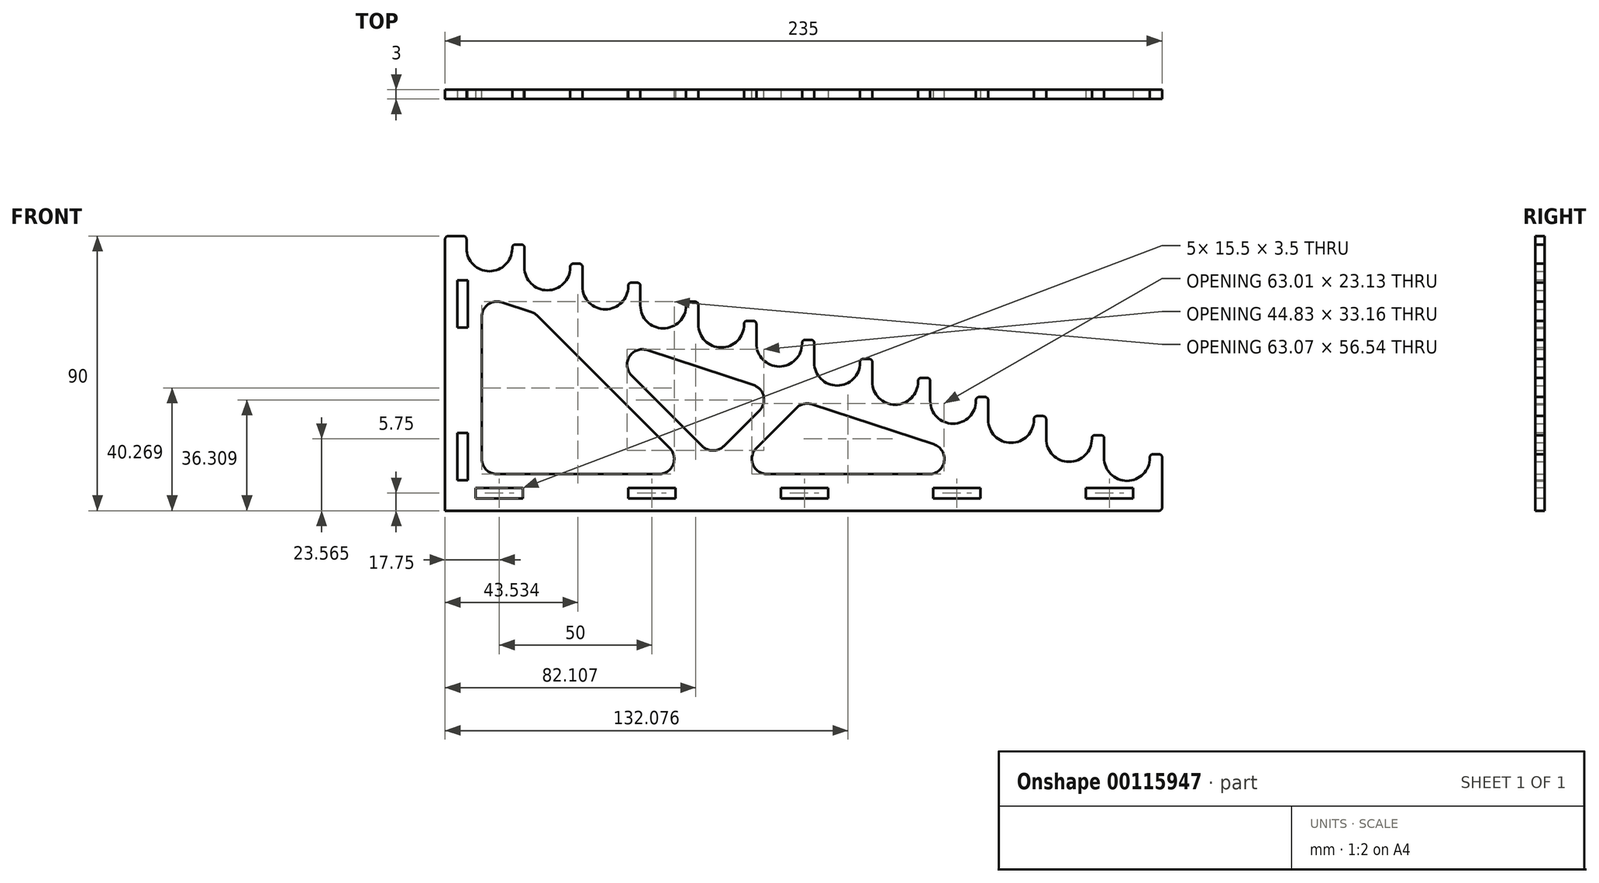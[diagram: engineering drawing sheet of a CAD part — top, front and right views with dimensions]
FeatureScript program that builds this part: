
annotation { "Feature Type Name" : "Feature", "Feature Type Description" : "" }
export const myFeature = defineFeature(function(context is Context, id is Id, definition is map)
    precondition{}
    {
        {
            var Q0;
            Q0=qCreatedBy(makeId("Front.planeOp"),FACE);
            var sketch = newSketch(context, id + "F0", { "sketchPlane" : qUnion([Q0])});
            skLineSegment(sketch, "E0", {"start": v(0, 0) * mm, "end": v(235, 0) * mm});
            skLineSegment(sketch, "E1", {"start": v(0, 0) * mm, "end": v(0, 90) * mm});
            skLineSegment(sketch, "E2", {"start": v(7, 90) * mm, "end": v(239.67, 13.52) * mm, "construction": true});
            skArc(sketch, "E3", {"start": v(7, 86) * mm, "mid": v(14.5, 78.5) * mm, "end": v(22, 86) * mm});
            skLineSegment(sketch, "E4", {"start": v(235, 17.53) * mm, "end": v(235, 0) * mm});
            skLineSegment(sketch, "E5", {"start": v(6, 90) * mm, "end": v(0, 90) * mm});
            skLineSegment(sketch, "E6", {"start": v(7, 86) * mm, "end": v(7, 89) * mm});
            skLineSegment(sketch, "E7.0", {"start": v(12, 17) * mm, "end": v(12, 63.56) * mm});
            skLineSegment(sketch, "E8.0", {"start": v(17, 12) * mm, "end": v(70.1, 12) * mm});
            skLineSegment(sketch, "E9.0", {"start": v(18.56, 68.3) * mm, "end": v(28.3, 65.1) * mm});
            skArc(sketch, "E10.filletArc", {"start": v(18.56, 68.3) * mm, "mid": v(14.07, 67.6) * mm, "end": v(12, 63.56) * mm});
            skArc(sketch, "E11.filletArc", {"start": v(12, 17) * mm, "mid": v(13.46, 13.46) * mm, "end": v(17, 12) * mm});
            skArc(sketch, "E12.filletArc", {"start": v(158.64, 12) * mm, "mid": v(163.58, 16.2) * mm, "end": v(160.2, 21.75) * mm});
            skLineSegment(sketch, "E13.1.0.0", {"start": v(26, 79.76) * mm, "end": v(26, 83.76) * mm});
            skArc(sketch, "E13.1.0.1", {"start": v(26, 79.76) * mm, "mid": v(33.5, 72.26) * mm, "end": v(41, 79.76) * mm});
            skLineSegment(sketch, "E13.2.0.0", {"start": v(45, 73.51) * mm, "end": v(45, 77.51) * mm});
            skArc(sketch, "E13.2.0.1", {"start": v(45, 73.51) * mm, "mid": v(52.5, 66.01) * mm, "end": v(60, 73.51) * mm});
            skLineSegment(sketch, "E13.direction1", {"start": v(7, 86) * mm, "end": v(26, 79.76) * mm, "construction": true});
            skLineSegment(sketch, "E14.0.3.0", {"start": v(64, 67.27) * mm, "end": v(64, 71.27) * mm});
            skArc(sketch, "E14.3.3.0", {"start": v(64, 67.27) * mm, "mid": v(71.5, 59.77) * mm, "end": v(79, 67.27) * mm});
            skLineSegment(sketch, "E14.0.4.0", {"start": v(83, 61.02) * mm, "end": v(83, 65.02) * mm});
            skArc(sketch, "E14.3.4.0", {"start": v(83, 61.02) * mm, "mid": v(90.5, 53.52) * mm, "end": v(98, 61.02) * mm});
            skLineSegment(sketch, "E14.0.5.0", {"start": v(102, 54.78) * mm, "end": v(102, 58.78) * mm});
            skArc(sketch, "E14.3.5.0", {"start": v(102, 54.78) * mm, "mid": v(109.5, 47.28) * mm, "end": v(117, 54.78) * mm});
            skLineSegment(sketch, "E14.0.6.0", {"start": v(121, 48.53) * mm, "end": v(121, 52.53) * mm});
            skArc(sketch, "E14.3.6.0", {"start": v(121, 48.53) * mm, "mid": v(128.5, 41.03) * mm, "end": v(136, 48.53) * mm});
            skLineSegment(sketch, "E14.0.7.0", {"start": v(140, 42.29) * mm, "end": v(140, 46.29) * mm});
            skArc(sketch, "E14.3.7.0", {"start": v(140, 42.29) * mm, "mid": v(147.5, 34.79) * mm, "end": v(155, 42.29) * mm});
            skLineSegment(sketch, "E14.0.8.0", {"start": v(159, 36.04) * mm, "end": v(159, 40.04) * mm});
            skArc(sketch, "E14.3.8.0", {"start": v(159, 36.04) * mm, "mid": v(166.5, 28.54) * mm, "end": v(174, 36.04) * mm});
            skLineSegment(sketch, "E14.0.9.0", {"start": v(178, 29.8) * mm, "end": v(178, 33.8) * mm});
            skArc(sketch, "E14.3.9.0", {"start": v(178, 29.8) * mm, "mid": v(185.5, 22.3) * mm, "end": v(193, 29.8) * mm});
            skLineSegment(sketch, "E14.0.10.0", {"start": v(197, 23.55) * mm, "end": v(197, 27.55) * mm});
            skArc(sketch, "E14.3.10.0", {"start": v(197, 23.55) * mm, "mid": v(204.5, 16.05) * mm, "end": v(212, 23.55) * mm});
            skLineSegment(sketch, "E14.0.11.0", {"start": v(216, 17.3) * mm, "end": v(216, 21.3) * mm});
            skArc(sketch, "E14.3.11.0", {"start": v(216, 17.3) * mm, "mid": v(223.5, 9.8) * mm, "end": v(231, 17.3) * mm});
            skLineSegment(sketch, "E15", {"start": v(235, 18.53) * mm, "end": v(12.69, 91.6) * mm, "construction": true});
            skLineSegment(sketch, "E16", {"start": v(234, 18.53) * mm, "end": v(232, 18.53) * mm});
            skLineSegment(sketch, "E17", {"start": v(231, 17.53) * mm, "end": v(231, 17.3) * mm});
            skLineSegment(sketch, "E18", {"start": v(216, 21.3) * mm, "end": v(216, 23.78) * mm});
            skLineSegment(sketch, "E19", {"start": v(215, 24.78) * mm, "end": v(213, 24.78) * mm});
            skLineSegment(sketch, "E20", {"start": v(212, 23.78) * mm, "end": v(212, 23.55) * mm});
            skLineSegment(sketch, "E21", {"start": v(197, 27.55) * mm, "end": v(197, 30.02) * mm});
            skLineSegment(sketch, "E22", {"start": v(196, 31.02) * mm, "end": v(194, 31.02) * mm});
            skLineSegment(sketch, "E23", {"start": v(193, 30.02) * mm, "end": v(193, 29.8) * mm});
            skLineSegment(sketch, "E24", {"start": v(178, 33.8) * mm, "end": v(178, 36.27) * mm});
            skLineSegment(sketch, "E25", {"start": v(177, 37.27) * mm, "end": v(175, 37.27) * mm});
            skLineSegment(sketch, "E26", {"start": v(174, 36.27) * mm, "end": v(174, 36.04) * mm});
            skLineSegment(sketch, "E27", {"start": v(159, 40.04) * mm, "end": v(159, 42.51) * mm});
            skLineSegment(sketch, "E28", {"start": v(158, 43.51) * mm, "end": v(156, 43.51) * mm});
            skLineSegment(sketch, "E29", {"start": v(155, 42.51) * mm, "end": v(155, 42.29) * mm});
            skLineSegment(sketch, "E30", {"start": v(140, 46.29) * mm, "end": v(140, 48.76) * mm});
            skLineSegment(sketch, "E31", {"start": v(139, 49.76) * mm, "end": v(137, 49.76) * mm});
            skLineSegment(sketch, "E32", {"start": v(136, 48.76) * mm, "end": v(136, 48.53) * mm});
            skLineSegment(sketch, "E33", {"start": v(121, 52.53) * mm, "end": v(121, 55) * mm});
            skLineSegment(sketch, "E34", {"start": v(120, 56) * mm, "end": v(118, 56) * mm});
            skLineSegment(sketch, "E35", {"start": v(117, 55) * mm, "end": v(117, 54.78) * mm});
            skLineSegment(sketch, "E36", {"start": v(102, 58.78) * mm, "end": v(102, 61.25) * mm});
            skLineSegment(sketch, "E37", {"start": v(101, 62.25) * mm, "end": v(99, 62.24) * mm});
            skLineSegment(sketch, "E38", {"start": v(98, 61.24) * mm, "end": v(98, 61.02) * mm});
            skLineSegment(sketch, "E39", {"start": v(83, 65.02) * mm, "end": v(83, 67.5) * mm});
            skLineSegment(sketch, "E40", {"start": v(82, 68.5) * mm, "end": v(80, 68.5) * mm});
            skLineSegment(sketch, "E41", {"start": v(79, 67.5) * mm, "end": v(79, 67.27) * mm});
            skLineSegment(sketch, "E42", {"start": v(64, 71.27) * mm, "end": v(64, 73.74) * mm});
            skLineSegment(sketch, "E43", {"start": v(63, 74.74) * mm, "end": v(61, 74.73) * mm});
            skLineSegment(sketch, "E44", {"start": v(60, 73.73) * mm, "end": v(60, 73.51) * mm});
            skLineSegment(sketch, "E45", {"start": v(45, 77.51) * mm, "end": v(45, 79.98) * mm});
            skLineSegment(sketch, "E46", {"start": v(44, 80.98) * mm, "end": v(42, 80.97) * mm});
            skLineSegment(sketch, "E47", {"start": v(41, 79.97) * mm, "end": v(41, 79.76) * mm});
            skLineSegment(sketch, "E48", {"start": v(26, 83.76) * mm, "end": v(26, 86.23) * mm});
            skLineSegment(sketch, "E49", {"start": v(25, 87.23) * mm, "end": v(23, 87.22) * mm});
            skLineSegment(sketch, "E50", {"start": v(22, 86.22) * mm, "end": v(22, 86) * mm});
            skPoint(sketch, "E51.visualSharp", {"position": v(235, 18.53) * mm});
            skArc(sketch, "E51.filletArc", {"start": v(235, 17.53) * mm, "mid": v(234.7, 18.24) * mm, "end": v(234, 18.53) * mm});
            skPoint(sketch, "E52.visualSharp", {"position": v(231, 18.53) * mm});
            skArc(sketch, "E52.filletArc", {"start": v(232, 18.53) * mm, "mid": v(231.3, 18.24) * mm, "end": v(231, 17.53) * mm});
            skPoint(sketch, "E53.visualSharp", {"position": v(216, 24.78) * mm});
            skArc(sketch, "E53.filletArc", {"start": v(216, 23.78) * mm, "mid": v(215.7, 24.49) * mm, "end": v(215, 24.78) * mm});
            skPoint(sketch, "E54.visualSharp", {"position": v(212, 24.78) * mm});
            skArc(sketch, "E54.filletArc", {"start": v(213, 24.78) * mm, "mid": v(212.3, 24.49) * mm, "end": v(212, 23.78) * mm});
            skPoint(sketch, "E55.visualSharp", {"position": v(197, 31.02) * mm});
            skArc(sketch, "E55.filletArc", {"start": v(197, 30.02) * mm, "mid": v(196.7, 30.73) * mm, "end": v(196, 31.02) * mm});
            skPoint(sketch, "E56.visualSharp", {"position": v(193, 31.02) * mm});
            skArc(sketch, "E56.filletArc", {"start": v(194, 31.02) * mm, "mid": v(193.3, 30.73) * mm, "end": v(193, 30.02) * mm});
            skPoint(sketch, "E57.visualSharp", {"position": v(178, 37.27) * mm});
            skArc(sketch, "E57.filletArc", {"start": v(178, 36.27) * mm, "mid": v(177.7, 36.98) * mm, "end": v(177, 37.27) * mm});
            skPoint(sketch, "E58.visualSharp", {"position": v(174, 37.27) * mm});
            skArc(sketch, "E58.filletArc", {"start": v(175, 37.27) * mm, "mid": v(174.3, 36.98) * mm, "end": v(174, 36.27) * mm});
            skPoint(sketch, "E59.visualSharp", {"position": v(159, 43.51) * mm});
            skArc(sketch, "E59.filletArc", {"start": v(159, 42.51) * mm, "mid": v(158.7, 43.22) * mm, "end": v(158, 43.51) * mm});
            skPoint(sketch, "E60.visualSharp", {"position": v(155, 43.51) * mm});
            skArc(sketch, "E60.filletArc", {"start": v(156, 43.51) * mm, "mid": v(155.3, 43.22) * mm, "end": v(155, 42.51) * mm});
            skPoint(sketch, "E61.visualSharp", {"position": v(140, 49.76) * mm});
            skArc(sketch, "E61.filletArc", {"start": v(140, 48.76) * mm, "mid": v(139.7, 49.47) * mm, "end": v(139, 49.76) * mm});
            skPoint(sketch, "E62.visualSharp", {"position": v(136, 49.76) * mm});
            skArc(sketch, "E62.filletArc", {"start": v(137, 49.76) * mm, "mid": v(136.3, 49.47) * mm, "end": v(136, 48.76) * mm});
            skPoint(sketch, "E63.visualSharp", {"position": v(121, 56) * mm});
            skArc(sketch, "E63.filletArc", {"start": v(121, 55) * mm, "mid": v(120.7, 55.71) * mm, "end": v(120, 56) * mm});
            skPoint(sketch, "E64.visualSharp", {"position": v(117, 56) * mm});
            skArc(sketch, "E64.filletArc", {"start": v(118, 56) * mm, "mid": v(117.3, 55.71) * mm, "end": v(117, 55) * mm});
            skPoint(sketch, "E65.visualSharp", {"position": v(102, 62.25) * mm});
            skArc(sketch, "E65.filletArc", {"start": v(102, 61.25) * mm, "mid": v(101.7, 61.95) * mm, "end": v(101, 62.25) * mm});
            skPoint(sketch, "E66.visualSharp", {"position": v(98, 62.23) * mm});
            skArc(sketch, "E66.filletArc", {"start": v(99, 62.24) * mm, "mid": v(98.3, 61.94) * mm, "end": v(98, 61.24) * mm});
            skPoint(sketch, "E67.visualSharp", {"position": v(83, 68.5) * mm});
            skArc(sketch, "E67.filletArc", {"start": v(83, 67.5) * mm, "mid": v(82.7, 68.2) * mm, "end": v(82, 68.5) * mm});
            skPoint(sketch, "E68.visualSharp", {"position": v(79, 68.5) * mm});
            skArc(sketch, "E68.filletArc", {"start": v(80, 68.5) * mm, "mid": v(79.3, 68.2) * mm, "end": v(79, 67.5) * mm});
            skPoint(sketch, "E69.visualSharp", {"position": v(64, 74.74) * mm});
            skArc(sketch, "E69.filletArc", {"start": v(64, 73.74) * mm, "mid": v(63.7, 74.44) * mm, "end": v(63, 74.74) * mm});
            skPoint(sketch, "E70.visualSharp", {"position": v(60, 74.72) * mm});
            skArc(sketch, "E70.filletArc", {"start": v(61, 74.73) * mm, "mid": v(60.3, 74.43) * mm, "end": v(60, 73.73) * mm});
            skPoint(sketch, "E71.visualSharp", {"position": v(45, 80.98) * mm});
            skArc(sketch, "E71.filletArc", {"start": v(45, 79.98) * mm, "mid": v(44.7, 80.69) * mm, "end": v(44, 80.98) * mm});
            skPoint(sketch, "E72.visualSharp", {"position": v(41, 80.97) * mm});
            skArc(sketch, "E72.filletArc", {"start": v(42, 80.97) * mm, "mid": v(41.3, 80.68) * mm, "end": v(41, 79.97) * mm});
            skPoint(sketch, "E73.visualSharp", {"position": v(26, 87.23) * mm});
            skArc(sketch, "E73.filletArc", {"start": v(26, 86.23) * mm, "mid": v(25.7, 86.93) * mm, "end": v(25, 87.23) * mm});
            skPoint(sketch, "E74.visualSharp", {"position": v(22, 87.21) * mm});
            skArc(sketch, "E74.filletArc", {"start": v(23, 87.22) * mm, "mid": v(22.3, 86.92) * mm, "end": v(22, 86.22) * mm});
            skPoint(sketch, "E75.visualSharp", {"position": v(7, 90) * mm});
            skArc(sketch, "E75.filletArc", {"start": v(7, 89) * mm, "mid": v(6.7, 89.7) * mm, "end": v(6, 90) * mm});
            skLineSegment(sketch, "E76", {"start": v(87.82, 12) * mm, "end": v(37.86, 61.96) * mm, "construction": true});
            skLineSegment(sketch, "E77", {"start": v(87.82, 12) * mm, "end": v(113.06, 37.24) * mm, "construction": true});
            skLineSegment(sketch, "E78.0", {"start": v(73.63, 20.54) * mm, "end": v(30.27, 63.89) * mm});
            skLineSegment(sketch, "E79.0", {"start": v(90.74, 14.74) * mm, "end": v(90.65, 14.83) * mm});
            skLineSegment(sketch, "E80.0", {"start": v(91.36, 21.2) * mm, "end": v(103.06, 32.9) * mm});
            skLineSegment(sketch, "E81.0", {"start": v(102.01, 20.54) * mm, "end": v(115.15, 33.67) * mm});
            skLineSegment(sketch, "E82.trimOffspring", {"start": v(66.22, 52.64) * mm, "end": v(101.09, 41.18) * mm});
            skLineSegment(sketch, "E83.trimOffspring", {"start": v(105.55, 12) * mm, "end": v(158.64, 12) * mm});
            skLineSegment(sketch, "E84.trimOffspring", {"start": v(84.29, 21.2) * mm, "end": v(61.12, 44.36) * mm});
            skLineSegment(sketch, "E85.trimOffspring", {"start": v(120.24, 34.88) * mm, "end": v(160.2, 21.75) * mm});
            skPoint(sketch, "E86.visualSharp", {"position": v(29.43, 64.73) * mm});
            skArc(sketch, "E86.filletArc", {"start": v(30.27, 63.89) * mm, "mid": v(29.36, 64.61) * mm, "end": v(28.3, 65.1) * mm});
            skPoint(sketch, "E87.visualSharp", {"position": v(46.28, 59.2) * mm});
            skArc(sketch, "E87.filletArc", {"start": v(66.22, 52.64) * mm, "mid": v(60.4, 50.51) * mm, "end": v(61.12, 44.36) * mm});
            skPoint(sketch, "E88.visualSharp", {"position": v(108.8, 38.64) * mm});
            skArc(sketch, "E88.filletArc", {"start": v(103.06, 32.9) * mm, "mid": v(104.39, 37.59) * mm, "end": v(101.09, 41.18) * mm});
            skPoint(sketch, "E89.visualSharp", {"position": v(117.32, 35.84) * mm});
            skArc(sketch, "E89.filletArc", {"start": v(120.24, 34.88) * mm, "mid": v(117.52, 35) * mm, "end": v(115.15, 33.67) * mm});
            skPoint(sketch, "E90.visualSharp", {"position": v(93.48, 12) * mm});
            skArc(sketch, "E90.filletArc", {"start": v(102.01, 20.54) * mm, "mid": v(100.93, 15.09) * mm, "end": v(105.55, 12) * mm});
            skPoint(sketch, "E91.visualSharp", {"position": v(87.82, 17.66) * mm});
            skArc(sketch, "E91.filletArc", {"start": v(84.29, 21.2) * mm, "mid": v(87.82, 19.73) * mm, "end": v(91.36, 21.2) * mm});
            skPoint(sketch, "E92.visualSharp", {"position": v(82.16, 12) * mm});
            skArc(sketch, "E92.filletArc", {"start": v(70.1, 12) * mm, "mid": v(74.71, 15.09) * mm, "end": v(73.63, 20.54) * mm});
            skSolve(sketch);
        }
        {
            var Q0;
            Q0=qSketchRegion(id+"F0",true);
            extrude(context, id + "F1", {"entities" : qUnion([Q0]), "depth" : 3 * mm});
        }
        {
            var Q0;
            Q0=makeQuery(id+"F1.opExtrude","SWEPT_EDGE",EDGE,{"disambiguationData":[OSD([sQuery(id+"F0.wireOp",EDGE,"E5"),sQuery(id+"F0.wireOp",EDGE,"E6")])]});
            var Q1;
            Q1=makeQuery(id+"F1.opExtrude","SWEPT_EDGE",EDGE,{"disambiguationData":[OSD([sQuery(id+"F0.wireOp",EDGE,"f5WcsviT-eBdv-jOtk-LFa1-m259dKIGtPj5"),sQuery(id+"F0.wireOp",EDGE,"7109644b-da97-4442-ba82-5f13c007bac0")])]});
            var Q2;
            Q2=makeQuery(id+"F1.opExtrude","SWEPT_EDGE",EDGE,{"disambiguationData":[OSD([sQuery(id+"F0.wireOp",EDGE,"f5WcsviT-eBdv-jOtk-LFa1-m259dKIGtPj5"),sQuery(id+"F0.wireOp",EDGE,"9TQmwsHQ-Kq4A-BqS7-9eDP-iYxJGyc13pck")])]});
            var Q3;
            Q3=makeQuery(id+"F1.opExtrude","SWEPT_EDGE",EDGE,{"disambiguationData":[OSD([sQuery(id+"F0.wireOp",EDGE,"ac84fd30-e2a6-4bf4-979c-238122ab8e38"),sQuery(id+"F0.wireOp",EDGE,"AsNxREgp-p4oo-jdf9-BHcI-YVDaj41r2qvn")])]});
            var Q4;
            Q4=makeQuery(id+"F1.opExtrude","SWEPT_EDGE",EDGE,{"disambiguationData":[OSD([sQuery(id+"F0.wireOp",EDGE,"ac84fd30-e2a6-4bf4-979c-238122ab8e38"),sQuery(id+"F0.wireOp",EDGE,"8448233a-de52-4eaa-82c2-632371ca7178")])]});
            var Q5;
            Q5=makeQuery(id+"F1.opExtrude","SWEPT_EDGE",EDGE,{"disambiguationData":[OSD([sQuery(id+"F0.wireOp",EDGE,"N8f9T7Of-BLLu-f8qQ-dwpx-mvwT7IFrPf0h"),sQuery(id+"F0.wireOp",EDGE,"2ceca206-df27-4c03-a48e-7652f30e0fab.trimOffspring")])]});
            var Q6;
            Q6=makeQuery(id+"F1.opExtrude","SWEPT_EDGE",EDGE,{"disambiguationData":[OSD([sQuery(id+"F0.wireOp",EDGE,"c6d8e859-939d-40aa-84c3-edd4eff7d0a0"),sQuery(id+"F0.wireOp",EDGE,"2ceca206-df27-4c03-a48e-7652f30e0fab.trimOffspring")])]});
            var Q7;
            Q7=makeQuery(id+"F1.opExtrude","SWEPT_EDGE",EDGE,{"disambiguationData":[OSD([sQuery(id+"F0.wireOp",EDGE,"E4"),sQuery(id+"F0.wireOp",EDGE,"3b0d8c0d-83ce-47f2-9aba-3b56bd8760bf.trimOffspring")])]});
            var Q8;
            Q8=makeQuery(id+"F1.opExtrude","SWEPT_EDGE",EDGE,{"disambiguationData":[OSD([sQuery(id+"F0.wireOp",EDGE,"ZcGVfwKi-gQVa-fUKh-N9YP-dPtnsNPX2cHW"),sQuery(id+"F0.wireOp",EDGE,"3b0d8c0d-83ce-47f2-9aba-3b56bd8760bf.trimOffspring")])]});
            var Q9;
            Q9=makeQuery(id+"F1.opExtrude","SWEPT_EDGE",EDGE,{"disambiguationData":[OSD([sQuery(id+"F0.wireOp",EDGE,"bdfd295d-5ed7-4b72-8697-4b4a761d33b8"),sQuery(id+"F0.wireOp",EDGE,"d0acfdc7-60d4-4c28-a21b-dc6c29154d0d")])]});
            var Q10;
            Q10=makeQuery(id+"F1.opExtrude","SWEPT_EDGE",EDGE,{"disambiguationData":[OSD([sQuery(id+"F0.wireOp",EDGE,"bdfd295d-5ed7-4b72-8697-4b4a761d33b8"),sQuery(id+"F0.wireOp",EDGE,"WVdz8BSc-ItTg-9hm4-jgHF-8DvA4EI1fQHK")])]});
            fillet(context, id + "F2", {"entities" : qUnion([Q0, Q1, Q2, Q3, Q4, Q5, Q6, Q7, Q8, Q9, Q10]), "radius" : 1 * mm, "tangentPropagation" : true, "allowEdgeOverflow" : false});
        }
        {
            var Q0;
            Q0=makeQuery(id+"F1.opExtrude","CAP_FACE",FACE,{"disambiguationData":[OSD([sQuery(id+"F0.wireOp",EDGE,"E0"),sQuery(id+"F0.wireOp",EDGE,"E1"),sQuery(id+"F0.wireOp",EDGE,"E3"),sQuery(id+"F0.wireOp",EDGE,"435fc08e-ad81-4076-899f-18b125047f18"),sQuery(id+"F0.wireOp",EDGE,"5f8505d8-a182-4fa0-9e64-1791f6f34801"),sQuery(id+"F0.wireOp",EDGE,"d325fad2-d954-4155-a3d0-cfd5ec8ad57f"),sQuery(id+"F0.wireOp",EDGE,"90493849-1ef6-4053-a3aa-90b6cb573290"),sQuery(id+"F0.wireOp",EDGE,"f5WcsviT-eBdv-jOtk-LFa1-m259dKIGtPj5"),sQuery(id+"F0.wireOp",EDGE,"9TQmwsHQ-Kq4A-BqS7-9eDP-iYxJGyc13pck"),sQuery(id+"F0.wireOp",EDGE,"ac84fd30-e2a6-4bf4-979c-238122ab8e38"),sQuery(id+"F0.wireOp",EDGE,"8448233a-de52-4eaa-82c2-632371ca7178"),sQuery(id+"F0.wireOp",EDGE,"c6d8e859-939d-40aa-84c3-edd4eff7d0a0"),sQuery(id+"F0.wireOp",EDGE,"bdfd295d-5ed7-4b72-8697-4b4a761d33b8"),sQuery(id+"F0.wireOp",EDGE,"d0acfdc7-60d4-4c28-a21b-dc6c29154d0d"),sQuery(id+"F0.wireOp",EDGE,"E4"),sQuery(id+"F0.wireOp",EDGE,"E5"),sQuery(id+"F0.wireOp",EDGE,"E6"),sQuery(id+"F0.wireOp",EDGE,"7109644b-da97-4442-ba82-5f13c007bac0"),sQuery(id+"F0.wireOp",EDGE,"AsNxREgp-p4oo-jdf9-BHcI-YVDaj41r2qvn"),sQuery(id+"F0.wireOp",EDGE,"N8f9T7Of-BLLu-f8qQ-dwpx-mvwT7IFrPf0h"),sQuery(id+"F0.wireOp",EDGE,"WVdz8BSc-ItTg-9hm4-jgHF-8DvA4EI1fQHK"),sQuery(id+"F0.wireOp",EDGE,"ZcGVfwKi-gQVa-fUKh-N9YP-dPtnsNPX2cHW"),sQuery(id+"F0.wireOp",EDGE,"2ceca206-df27-4c03-a48e-7652f30e0fab.trimOffspring"),sQuery(id+"F0.wireOp",EDGE,"3b0d8c0d-83ce-47f2-9aba-3b56bd8760bf.trimOffspring"),sQuery(id+"F0.wireOp",EDGE,"E7.0"),sQuery(id+"F0.wireOp",EDGE,"E8.0"),sQuery(id+"F0.wireOp",EDGE,"E9.0"),sQuery(id+"F0.wireOp",EDGE,"E10.filletArc"),sQuery(id+"F0.wireOp",EDGE,"E11.filletArc"),sQuery(id+"F0.wireOp",EDGE,"E12.filletArc")])],"isStart":false});
            var sketch = newSketch(context, id + "F3", { "sketchPlane" : qUnion([Q0])});
            skLineSegment(sketch, "E93.bottom", {"start": v(10, 7.5) * mm, "end": v(25.5, 7.5) * mm});
            skLineSegment(sketch, "E93.top", {"start": v(10, 4) * mm, "end": v(25.5, 4) * mm});
            skLineSegment(sketch, "E93.left", {"start": v(10, 7.5) * mm, "end": v(10, 4) * mm});
            skLineSegment(sketch, "E93.right", {"start": v(25.5, 7.5) * mm, "end": v(25.5, 4) * mm});
            skLineSegment(sketch, "E94.bottom", {"start": v(4, 25.5) * mm, "end": v(7.5, 25.5) * mm});
            skLineSegment(sketch, "E94.top", {"start": v(4, 10) * mm, "end": v(7.5, 10) * mm});
            skLineSegment(sketch, "E94.left", {"start": v(4, 25.5) * mm, "end": v(4, 10) * mm});
            skLineSegment(sketch, "E94.right", {"start": v(7.5, 25.5) * mm, "end": v(7.5, 10) * mm});
            skLineSegment(sketch, "E95.bottom", {"start": v(4, 75.5) * mm, "end": v(7.5, 75.5) * mm});
            skLineSegment(sketch, "E95.top", {"start": v(4, 60) * mm, "end": v(7.5, 60) * mm});
            skLineSegment(sketch, "E95.left", {"start": v(4, 75.5) * mm, "end": v(4, 60) * mm});
            skLineSegment(sketch, "E95.right", {"start": v(7.5, 75.5) * mm, "end": v(7.5, 60) * mm});
            skLineSegment(sketch, "E96.1.0.0", {"start": v(60, 4) * mm, "end": v(75.5, 4) * mm});
            skLineSegment(sketch, "E96.1.0.1", {"start": v(60, 7.5) * mm, "end": v(75.5, 7.5) * mm});
            skLineSegment(sketch, "E96.1.0.2", {"start": v(75.5, 7.5) * mm, "end": v(75.5, 4) * mm});
            skLineSegment(sketch, "E96.1.0.3", {"start": v(60, 7.5) * mm, "end": v(60, 4) * mm});
            skLineSegment(sketch, "E96.2.0.0", {"start": v(110, 4) * mm, "end": v(125.5, 4) * mm});
            skLineSegment(sketch, "E96.2.0.1", {"start": v(110, 7.5) * mm, "end": v(125.5, 7.5) * mm});
            skLineSegment(sketch, "E96.2.0.2", {"start": v(125.5, 7.5) * mm, "end": v(125.5, 4) * mm});
            skLineSegment(sketch, "E96.2.0.3", {"start": v(110, 7.5) * mm, "end": v(110, 4) * mm});
            skLineSegment(sketch, "E96.3.0.0", {"start": v(160, 4) * mm, "end": v(175.5, 4) * mm});
            skLineSegment(sketch, "E96.3.0.1", {"start": v(160, 7.5) * mm, "end": v(175.5, 7.5) * mm});
            skLineSegment(sketch, "E96.3.0.2", {"start": v(175.5, 7.5) * mm, "end": v(175.5, 4) * mm});
            skLineSegment(sketch, "E96.3.0.3", {"start": v(160, 7.5) * mm, "end": v(160, 4) * mm});
            skLineSegment(sketch, "E96.4.0.0", {"start": v(210, 4) * mm, "end": v(225.5, 4) * mm});
            skLineSegment(sketch, "E96.4.0.1", {"start": v(210, 7.5) * mm, "end": v(225.5, 7.5) * mm});
            skLineSegment(sketch, "E96.4.0.2", {"start": v(225.5, 7.5) * mm, "end": v(225.5, 4) * mm});
            skLineSegment(sketch, "E96.4.0.3", {"start": v(210, 7.5) * mm, "end": v(210, 4) * mm});
            skLineSegment(sketch, "E96.direction1", {"start": v(10, 4) * mm, "end": v(60, 4) * mm, "construction": true});
            skSolve(sketch);
        }
        {
            var Q0;
            Q0=qSketchRegion(id+"F3",true);
            extrude(context, id + "F4", {"entities" : qUnion([Q0]), "operationType" : NewBodyOperationType.REMOVE, "oppositeDirection" : true, "depth" : 25 * mm});
        }
    });
